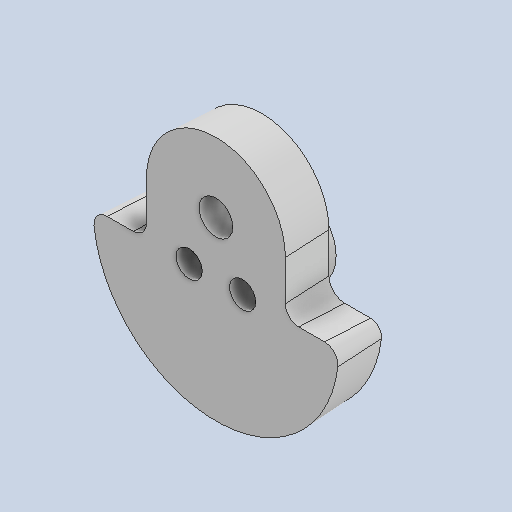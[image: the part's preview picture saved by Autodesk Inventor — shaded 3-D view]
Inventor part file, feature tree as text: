
AUTODESK INVENTOR PART (.ipt)
format: ipt  version: 2023 (Build 270158000, 158)  size: 499,712 bytes
history: native  units: in
note: dims shown in document units (in); Inventor stores cm internally (conversion verified against a paired STEP export)
features: extrude x5, draft x2, sketch x1, fillet x1
ambient origin geometry x8: Origin, YZ Plane, XZ Plane, XY Plane, X Axis, Y Axis, Z Axis, Center Point
bodies: Body1 (feature_tree)
feature tree (9):
  sketch  "Sketch1"  dims[d3=0.866in d15=0.75in d20=0.316in d37=0.75in d44=0.125in d52=0.245in d57=0.74in d58=0.75in d59=0.0in d60=0.32in d61=0.0in d62=1.5in d63=0.0in d64=1.5in d65=0.0in d66=0.375in d67=0.0in d68=0.125in d70=0.135in d71=0.0206in d72=0.0412in d73=1.15in]
  extrude  "Extrusion9"  Depth=0.125in
  extrude  "Extrusion10"  Depth=0.125in
  extrude  "Extrusion11"  Depth=0.125in
  extrude  "Extrusion12"  Depth=0.125in
  extrude  "Extrusion13"  Depth=0.125in
  fillet  "Fillet2"  Radius=0.75in
  draft  "FaceDraft1"
  draft  "FaceDraft2"
